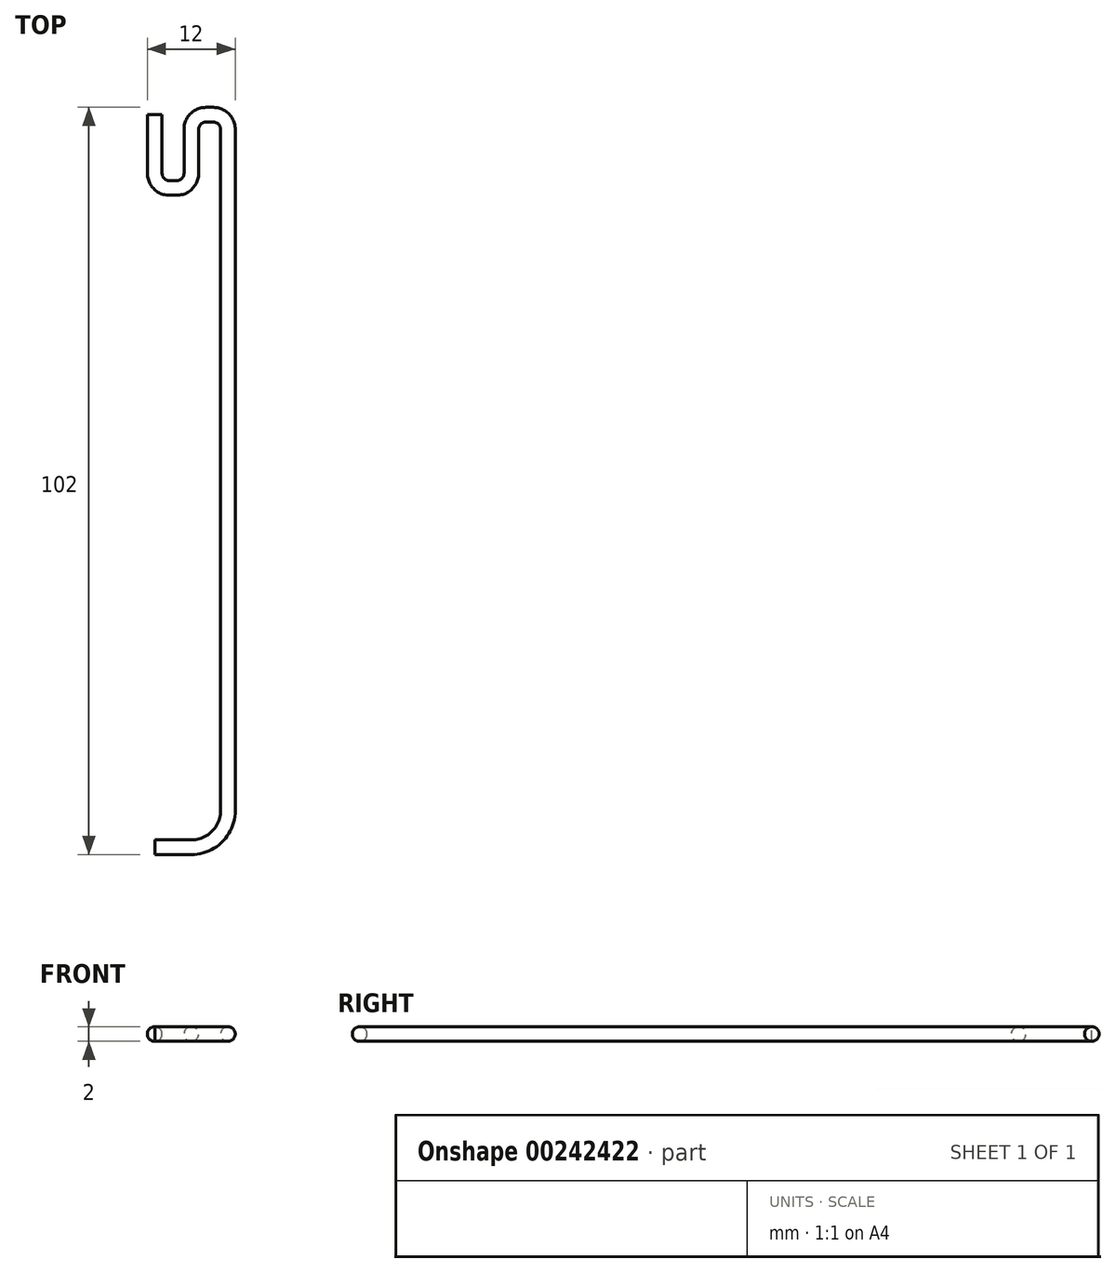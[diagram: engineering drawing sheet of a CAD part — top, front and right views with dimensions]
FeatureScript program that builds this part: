
annotation { "Feature Type Name" : "Feature", "Feature Type Description" : "" }
export const myFeature = defineFeature(function(context is Context, id is Id, definition is map)
    precondition{}
    {
        {
            var Q0;
            Q0=qCreatedBy(makeId("Top.planeOp"),FACE);
            var sketch = newSketch(context, id + "F0", { "sketchPlane" : qUnion([Q0])});
            skLineSegment(sketch, "E0", {"start": v(-73.47, 100) * mm, "end": v(-73.47, 92) * mm});
            skLineSegment(sketch, "E1", {"start": v(-71.47, 90) * mm, "end": v(-70.47, 90) * mm});
            skLineSegment(sketch, "E2", {"start": v(-68.47, 92) * mm, "end": v(-68.47, 98) * mm});
            skLineSegment(sketch, "E3", {"start": v(-66.47, 100) * mm, "end": v(-65.47, 100) * mm});
            skLineSegment(sketch, "E4", {"start": v(-63.47, 98) * mm, "end": v(-63.47, 5) * mm});
            skLineSegment(sketch, "E5", {"start": v(-68.47, 0) * mm, "end": v(-73.47, 0) * mm});
            skPoint(sketch, "E6.visualSharp", {"position": v(-73.47, 90) * mm});
            skArc(sketch, "E6.filletArc", {"start": v(-73.47, 92) * mm, "mid": v(-72.88, 90.59) * mm, "end": v(-71.47, 90) * mm});
            skPoint(sketch, "E7.visualSharp", {"position": v(-68.47, 90) * mm});
            skArc(sketch, "E7.filletArc", {"start": v(-70.47, 90) * mm, "mid": v(-69.06, 90.59) * mm, "end": v(-68.47, 92) * mm});
            skPoint(sketch, "E8.visualSharp", {"position": v(-68.47, 100) * mm});
            skArc(sketch, "E8.filletArc", {"start": v(-66.47, 100) * mm, "mid": v(-67.88, 99.41) * mm, "end": v(-68.47, 98) * mm});
            skPoint(sketch, "E9.visualSharp", {"position": v(-63.47, 100) * mm});
            skArc(sketch, "E9.filletArc", {"start": v(-63.47, 98) * mm, "mid": v(-64.06, 99.41) * mm, "end": v(-65.47, 100) * mm});
            skPoint(sketch, "E10.visualSharp", {"position": v(-63.47, 0) * mm});
            skArc(sketch, "E10.filletArc", {"start": v(-68.47, 0) * mm, "mid": v(-64.93, 1.46) * mm, "end": v(-63.47, 5) * mm});
            skSolve(sketch);
        }
        {
            var Q0;
            Q0=qCreatedBy(makeId("Front.planeOp"),FACE);
            var Q1;
            Q1=sQuery(id+"F0.wireOp",VERTEX,"E0.start");
            cPlane(context, id + "F1", {"entities" : qUnion([Q0, Q1]), "cplaneType" : CPlaneType.PLANE_POINT, "offset" : 25 * mm, "width" : 150 * mm, "height" : 150 * mm});
        }
        {
            var Q0;
            Q0=qCreatedBy(id+"F1.planeOp",FACE);
            var sketch = newSketch(context, id + "F2", { "sketchPlane" : qUnion([Q0])});
            skPoint(sketch, "E11.0", {"position": v(-73.47, 0) * mm});
            skCircle(sketch, "E12", {"center": v(-73.47, 0) * mm, "radius": 1 * mm});
            skSolve(sketch);
        }
        {
            var Q0;
            Q0=makeQuery(id+"F2.imprint","IMPRINT",FACE,{"disambiguationData":[TD([[makeQuery(id+"F2.imprint","IMPRINT",EDGE,{"derivedFrom":sQuery(id+"F2.wireOp",EDGE,"E12")}),1.0]])]});
            var Q1;
            Q1 = qSketchRegion(id + "FfLJgRCsmtqGtjr_1", true);
            var Q2;
            Q2=sQuery(id+"F2.wireOp",EDGE,"E12");
            var Q3;
            Q3=sQuery(id+"F0.wireOp",EDGE,"E0");
            var Q4;
            Q4=sQuery(id+"F0.wireOp",EDGE,"E6.filletArc");
            var Q5;
            Q5=sQuery(id+"F0.wireOp",EDGE,"E1");
            var Q6;
            Q6=sQuery(id+"F0.wireOp",EDGE,"E7.filletArc");
            var Q7;
            Q7=sQuery(id+"F0.wireOp",EDGE,"E2");
            var Q8;
            Q8=sQuery(id+"F0.wireOp",EDGE,"E8.filletArc");
            var Q9;
            Q9=sQuery(id+"F0.wireOp",EDGE,"E3");
            var Q10;
            Q10=sQuery(id+"F0.wireOp",EDGE,"E9.filletArc");
            var Q11;
            Q11=sQuery(id+"F0.wireOp",EDGE,"E4");
            var Q12;
            Q12=sQuery(id+"F0.wireOp",EDGE,"E10.filletArc");
            var Q13;
            Q13=sQuery(id+"F0.wireOp",EDGE,"E5");
            sweep(context, id + "F3", {"profiles" : qUnion([Q0, Q1]), "surfaceProfiles" : qUnion([Q2]), "path" : qUnion([Q3, Q4, Q5, Q6, Q7, Q8, Q9, Q10, Q11, Q12, Q13])});
        }
    });
